# Revit family: Shower-Valves_and_Controls-KOHLER-HiFlow_Rite-Temp-K-2971
name_source: partatom
category: Plumbing Fixtures
revit_build: Autodesk Revit 2015 (Build: 20140606_1530(x64)
units: mm (PartAtom-declared; Revit-internal decimal feet)

## types (1)
- Pressure-balancing single-handle valve
    ADA Compliant = Yes
    Assembly Code = D2020
    CW Connection = Yes
    Cold Water Inlet = Cold Water Inlet
    Date Modified = 02/07/2019
    Default Elevation = 36"
    Description = HiFlow Rite-Temp 3/4 inch pressure-balancing single-handle with screwdriver stops
    Finish = Kohler-Metal-Brass
    Flow Rate = 13 GPM
    HW Connection = Yes
    Height = 6"
    Hot Water Inlet = Hot Water Inlet
    Length = 2 1/4"
    Manufacturer = KOHLER Co.
    MasterFormat 1995 = 154300
    MasterFormat 2004 = 22.11.00
    Material = Brass construction
    Model = K-2971-KS-NA
    Pressure = 45.00 psi
    Product Documentation Link = https://www.us.kohler.com
    Product Name = Rite-Temp
    Product Page URL = http://www.us.kohler.com
    Tempered Water Outlet = Tempered Water Outlet
    URL = https://www.us.kohler.com
    Vent Connection = No
    Waste Connection = No
    Waste Water Outlet = Waste Water Outlet
    WaterSense Certified = No
    Width = 8"

## geometry (parser evidence)
native form markers: Sweep x7
no freeform markers — native parametric forms only
